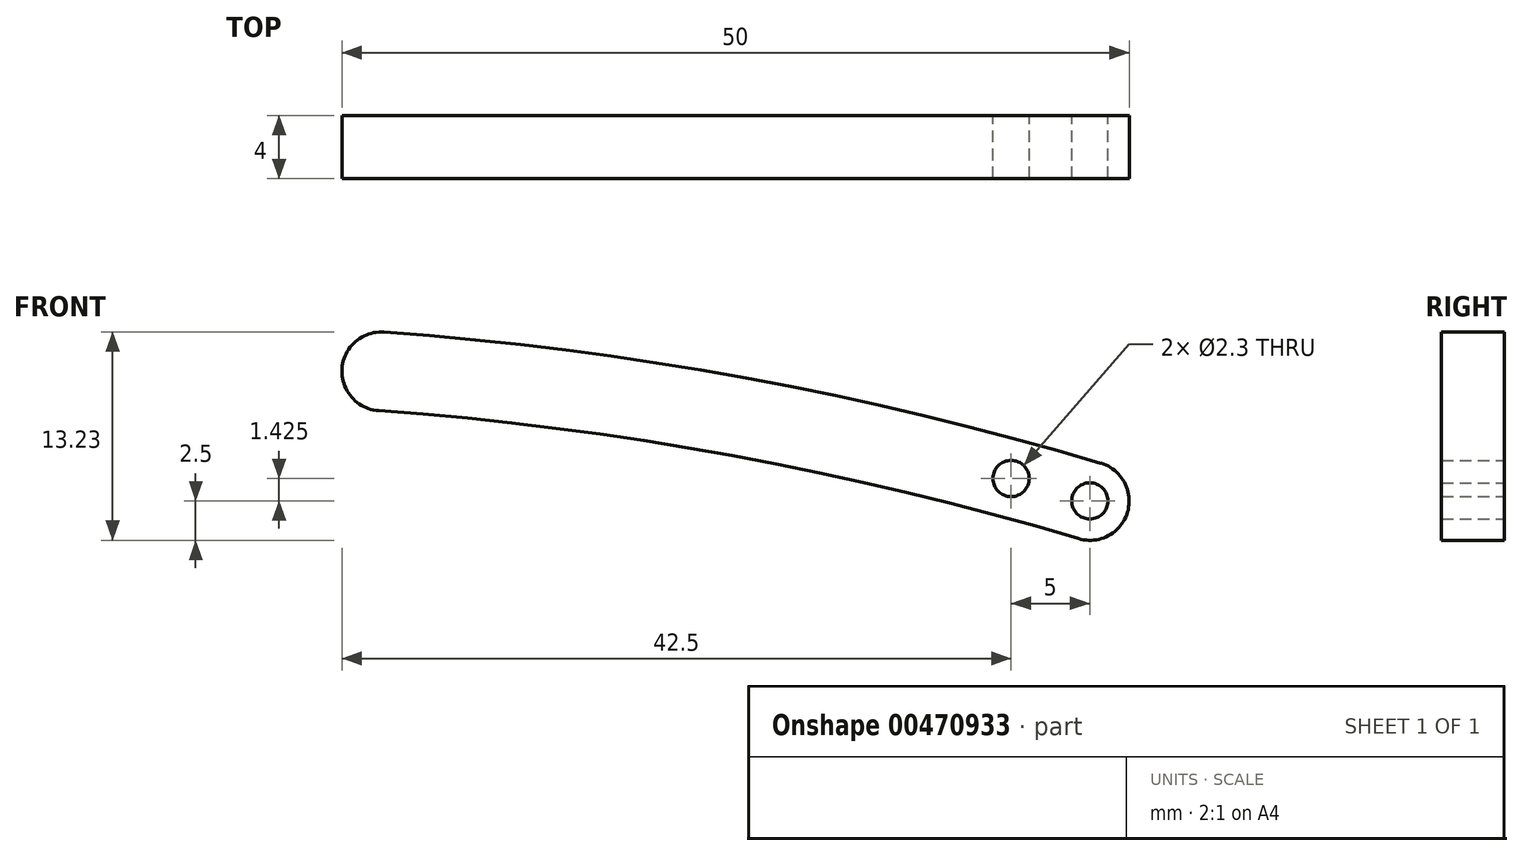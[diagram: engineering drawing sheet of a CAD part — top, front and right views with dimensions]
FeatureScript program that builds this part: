
annotation { "Feature Type Name" : "Feature", "Feature Type Description" : "" }
export const myFeature = defineFeature(function(context is Context, id is Id, definition is map)
    precondition{}
    {
        {
            var Q0;
            Q0=qCreatedBy(makeId("Front.planeOp"),FACE);
            var sketch = newSketch(context, id + "F0", { "sketchPlane" : qUnion([Q0])});
            skCircle(sketch, "E0", {"center": v(0, 0) * mm, "radius": 1.15 * mm});
            skCircle(sketch, "E1", {"center": v(-5, 1.42) * mm, "radius": 1.15 * mm});
            skArc(sketch, "E2", {"start": v(0, 0) * mm, "mid": v(-22.28, 5.34) * mm, "end": v(-45, 8.23) * mm});
            skArc(sketch, "E3.0", {"start": v(0.71, 2.4) * mm, "mid": v(-21.83, 7.8) * mm, "end": v(-44.82, 10.72) * mm});
            skArc(sketch, "E4.0", {"start": v(-0.71, -2.4) * mm, "mid": v(-22.72, 2.88) * mm, "end": v(-45.18, 5.74) * mm});
            skArc(sketch, "E5", {"start": v(-44.82, 10.72) * mm, "mid": v(-47.5, 8.4) * mm, "end": v(-45.18, 5.74) * mm});
            skArc(sketch, "E6", {"start": v(-0.71, -2.4) * mm, "mid": v(2.4, -0.71) * mm, "end": v(0.71, 2.4) * mm});
            skSolve(sketch);
        }
        {
            var Q0;
            Q0=qSketchRegion(id+"F0",true);
            extrude(context, id + "F1", {"entities" : qUnion([Q0]), "depth" : 4 * mm});
        }
    });
